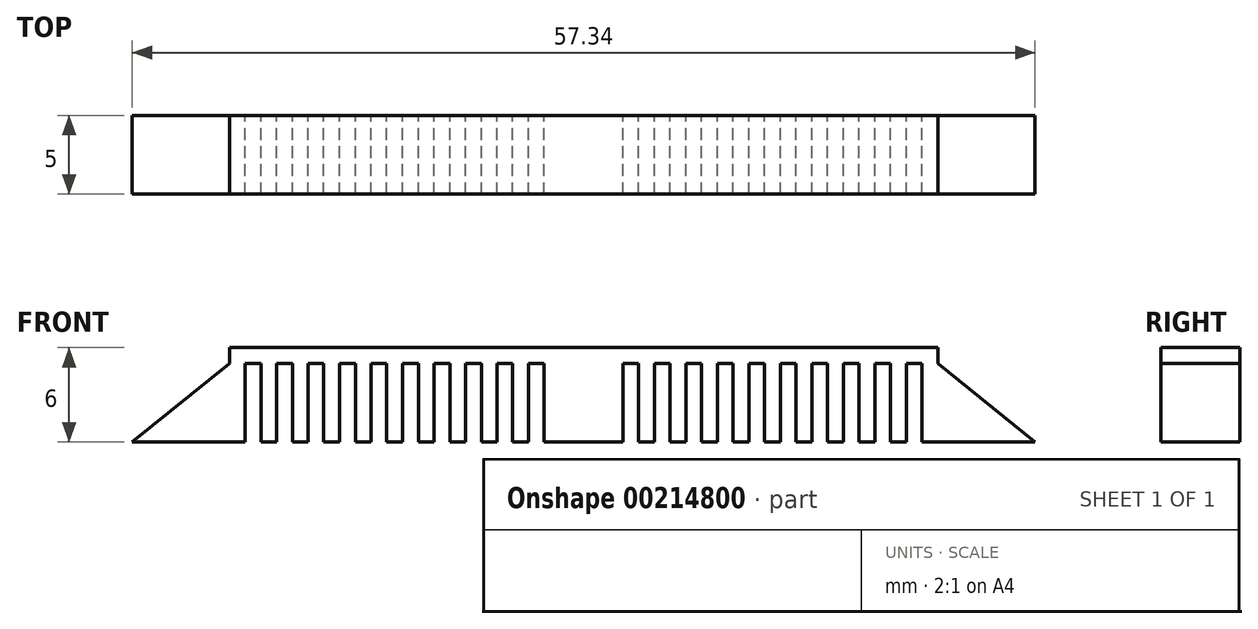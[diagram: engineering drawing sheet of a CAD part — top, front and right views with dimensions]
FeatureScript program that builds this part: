
annotation { "Feature Type Name" : "Feature", "Feature Type Description" : "" }
export const myFeature = defineFeature(function(context is Context, id is Id, definition is map)
    precondition{}
    {
        {
            var Q0;
            Q0=qCreatedBy(makeId("Front.planeOp"),FACE);
            var sketch = newSketch(context, id + "F0", { "sketchPlane" : qUnion([Q0])});
            skLineSegment(sketch, "E0.bottom", {"start": v(-21.5, 0) * mm, "end": v(-6.5, 0) * mm});
            skLineSegment(sketch, "E0.top", {"start": v(-22.5, 1) * mm, "end": v(22.5, 1) * mm});
            skLineSegment(sketch, "E0.left", {"start": v(-22.5, 0) * mm, "end": v(-22.5, 1) * mm});
            skLineSegment(sketch, "E0.right", {"start": v(22.5, 0) * mm, "end": v(22.5, 1) * mm});
            skLineSegment(sketch, "E1.top", {"start": v(-6.5, -5) * mm, "end": v(-5.5, -5) * mm});
            skLineSegment(sketch, "E1.left", {"start": v(-6.5, 0) * mm, "end": v(-6.5, -5) * mm});
            skLineSegment(sketch, "E1.right", {"start": v(2.5, 0) * mm, "end": v(2.5, -5) * mm});
            skLineSegment(sketch, "E2.trimOffspring", {"start": v(2.5, 0) * mm, "end": v(3.5, 0) * mm});
            skLineSegment(sketch, "E3.top", {"start": v(-20.5, -5) * mm, "end": v(-19.5, -5) * mm});
            skLineSegment(sketch, "E3.left", {"start": v(-19.5, 0) * mm, "end": v(-19.5, -5) * mm});
            skLineSegment(sketch, "E3.right", {"start": v(-20.5, 0) * mm, "end": v(-20.5, -5) * mm});
            skLineSegment(sketch, "E4.top", {"start": v(-18.5, -5) * mm, "end": v(-17.5, -5) * mm});
            skLineSegment(sketch, "E4.left", {"start": v(-18.5, 0) * mm, "end": v(-18.5, -5) * mm});
            skLineSegment(sketch, "E4.right", {"start": v(-17.5, 0) * mm, "end": v(-17.5, -5) * mm});
            skLineSegment(sketch, "E5.top", {"start": v(-16.5, -5) * mm, "end": v(-15.5, -5) * mm});
            skLineSegment(sketch, "E5.left", {"start": v(-16.5, 0) * mm, "end": v(-16.5, -5) * mm});
            skLineSegment(sketch, "E5.right", {"start": v(-15.5, 0) * mm, "end": v(-15.5, -5) * mm});
            skLineSegment(sketch, "E6.top", {"start": v(-14.5, -5) * mm, "end": v(-13.5, -5) * mm});
            skLineSegment(sketch, "E6.left", {"start": v(-14.5, 0) * mm, "end": v(-14.5, -5) * mm});
            skLineSegment(sketch, "E6.right", {"start": v(-13.5, 0) * mm, "end": v(-13.5, -5) * mm});
            skLineSegment(sketch, "E7.top", {"start": v(-12.5, -5) * mm, "end": v(-11.5, -5) * mm});
            skLineSegment(sketch, "E7.left", {"start": v(-12.5, 0) * mm, "end": v(-12.5, -5) * mm});
            skLineSegment(sketch, "E7.right", {"start": v(-11.5, 0) * mm, "end": v(-11.5, -5) * mm});
            skLineSegment(sketch, "E8.top", {"start": v(-10.5, -5) * mm, "end": v(-9.5, -5) * mm});
            skLineSegment(sketch, "E8.left", {"start": v(-10.5, 0) * mm, "end": v(-10.5, -5) * mm});
            skLineSegment(sketch, "E8.right", {"start": v(-9.5, 0) * mm, "end": v(-9.5, -5) * mm});
            skLineSegment(sketch, "E9.top", {"start": v(-8.5, -5) * mm, "end": v(-7.5, -5) * mm});
            skLineSegment(sketch, "E9.left", {"start": v(-7.5, 0) * mm, "end": v(-7.5, -5) * mm});
            skLineSegment(sketch, "E9.right", {"start": v(-8.5, 0) * mm, "end": v(-8.5, -5) * mm});
            skLineSegment(sketch, "E10", {"start": v(-21.5, 0) * mm, "end": v(-21.5, -5) * mm});
            skLineSegment(sketch, "E11", {"start": v(-21.5, -5) * mm, "end": v(-28.67, -5) * mm});
            skLineSegment(sketch, "E12", {"start": v(-28.67, -5) * mm, "end": v(-22.5, 0) * mm});
            skLineSegment(sketch, "E13", {"start": v(-5.5, -5) * mm, "end": v(-5.5, 0) * mm});
            skLineSegment(sketch, "E14", {"start": v(-5.5, 0) * mm, "end": v(-4.5, 0) * mm});
            skLineSegment(sketch, "E15", {"start": v(-4.5, 0) * mm, "end": v(-4.5, -5) * mm});
            skLineSegment(sketch, "E16.trimOffspring", {"start": v(-4.5, -5) * mm, "end": v(-3.5, -5) * mm});
            skLineSegment(sketch, "E17", {"start": v(-3.5, -5) * mm, "end": v(-3.5, 0) * mm});
            skLineSegment(sketch, "E18", {"start": v(-3.5, 0) * mm, "end": v(-2.5, 0) * mm});
            skLineSegment(sketch, "E19", {"start": v(-2.5, 0) * mm, "end": v(-2.5, -5) * mm});
            skLineSegment(sketch, "E20.trimOffspring", {"start": v(-2.5, -5) * mm, "end": v(2.5, -5) * mm});
            skLineSegment(sketch, "E21", {"start": v(22.5, 0) * mm, "end": v(28.67, -5) * mm});
            skLineSegment(sketch, "E22", {"start": v(28.67, -5) * mm, "end": v(21.5, -5) * mm});
            skLineSegment(sketch, "E23", {"start": v(20.5, -5) * mm, "end": v(20.5, 0) * mm});
            skLineSegment(sketch, "E24", {"start": v(19.5, 0) * mm, "end": v(18.5, 0) * mm});
            skLineSegment(sketch, "E25", {"start": v(18.5, 0) * mm, "end": v(18.5, -5) * mm});
            skLineSegment(sketch, "E26", {"start": v(18.5, -5) * mm, "end": v(17.5, -5) * mm});
            skLineSegment(sketch, "E27", {"start": v(17.5, -5) * mm, "end": v(17.5, 0) * mm});
            skLineSegment(sketch, "E28", {"start": v(17.5, 0) * mm, "end": v(16.5, 0) * mm});
            skLineSegment(sketch, "E29", {"start": v(16.5, 0) * mm, "end": v(16.5, -5) * mm});
            skLineSegment(sketch, "E30", {"start": v(16.5, -5) * mm, "end": v(15.5, -5) * mm});
            skLineSegment(sketch, "E31", {"start": v(15.5, -5) * mm, "end": v(15.5, 0) * mm});
            skLineSegment(sketch, "E32", {"start": v(15.5, 0) * mm, "end": v(14.5, 0) * mm});
            skLineSegment(sketch, "E33", {"start": v(14.5, 0) * mm, "end": v(14.5, -5) * mm});
            skLineSegment(sketch, "E34", {"start": v(14.5, -5) * mm, "end": v(13.5, -5) * mm});
            skLineSegment(sketch, "E35", {"start": v(13.5, -5) * mm, "end": v(13.5, 0) * mm});
            skLineSegment(sketch, "E36", {"start": v(13.5, 0) * mm, "end": v(12.5, 0) * mm});
            skLineSegment(sketch, "E37", {"start": v(12.5, 0) * mm, "end": v(12.5, -5) * mm});
            skLineSegment(sketch, "E38", {"start": v(12.5, -5) * mm, "end": v(11.5, -5) * mm});
            skLineSegment(sketch, "E39", {"start": v(11.5, -5) * mm, "end": v(11.5, 0) * mm});
            skLineSegment(sketch, "E40", {"start": v(11.5, 0) * mm, "end": v(10.5, 0) * mm});
            skLineSegment(sketch, "E41", {"start": v(10.5, 0) * mm, "end": v(10.5, -5) * mm});
            skLineSegment(sketch, "E42", {"start": v(10.5, -5) * mm, "end": v(9.5, -5) * mm});
            skLineSegment(sketch, "E43", {"start": v(9.5, -5) * mm, "end": v(9.5, 0) * mm});
            skLineSegment(sketch, "E44", {"start": v(9.5, 0) * mm, "end": v(8.5, 0) * mm});
            skLineSegment(sketch, "E45", {"start": v(8.5, 0) * mm, "end": v(8.5, -5) * mm});
            skLineSegment(sketch, "E46", {"start": v(8.5, -5) * mm, "end": v(7.5, -5) * mm});
            skLineSegment(sketch, "E47", {"start": v(7.5, -5) * mm, "end": v(7.5, 0) * mm});
            skLineSegment(sketch, "E48", {"start": v(7.5, 0) * mm, "end": v(6.5, 0) * mm});
            skLineSegment(sketch, "E49", {"start": v(6.5, 0) * mm, "end": v(6.5, -5) * mm});
            skLineSegment(sketch, "E50", {"start": v(6.5, -5) * mm, "end": v(5.5, -5) * mm});
            skLineSegment(sketch, "E51", {"start": v(5.5, -5) * mm, "end": v(5.5, 0) * mm});
            skLineSegment(sketch, "E52", {"start": v(5.5, 0) * mm, "end": v(4.5, 0) * mm});
            skLineSegment(sketch, "E53", {"start": v(4.5, 0) * mm, "end": v(4.5, -5) * mm});
            skLineSegment(sketch, "E54", {"start": v(4.5, -5) * mm, "end": v(3.5, -5) * mm});
            skLineSegment(sketch, "E55", {"start": v(3.5, -5) * mm, "end": v(3.5, 0) * mm});
            skLineSegment(sketch, "E56", {"start": v(18.5, 0) * mm, "end": v(19.5, 0) * mm});
            skLineSegment(sketch, "E57", {"start": v(19.5, 0) * mm, "end": v(19.5, -5) * mm});
            skLineSegment(sketch, "E58", {"start": v(19.5, -5) * mm, "end": v(20.5, -5) * mm});
            skLineSegment(sketch, "E59", {"start": v(21.5, -5) * mm, "end": v(21.5, 0) * mm});
            skLineSegment(sketch, "E60.trimOffspring", {"start": v(4.5, 0) * mm, "end": v(5.5, 0) * mm});
            skLineSegment(sketch, "E61.trimOffspring", {"start": v(6.5, 0) * mm, "end": v(7.5, 0) * mm});
            skLineSegment(sketch, "E62.trimOffspring", {"start": v(8.5, 0) * mm, "end": v(9.5, 0) * mm});
            skLineSegment(sketch, "E63.trimOffspring", {"start": v(10.5, 0) * mm, "end": v(11.5, 0) * mm});
            skLineSegment(sketch, "E64.trimOffspring", {"start": v(12.5, 0) * mm, "end": v(13.5, 0) * mm});
            skLineSegment(sketch, "E65.trimOffspring", {"start": v(14.5, 0) * mm, "end": v(15.5, 0) * mm});
            skLineSegment(sketch, "E66.trimOffspring", {"start": v(16.5, 0) * mm, "end": v(17.5, 0) * mm});
            skLineSegment(sketch, "E67.trimOffspring", {"start": v(20.5, 0) * mm, "end": v(21.5, 0) * mm});
            skSolve(sketch);
        }
        {
            var Q0;
            Q0 = qSketchRegion(id + "F0", true);
            extrude(context, id + "F1", {"entities" : qUnion([Q0]), "depth" : 5 * mm});
        }
    });
